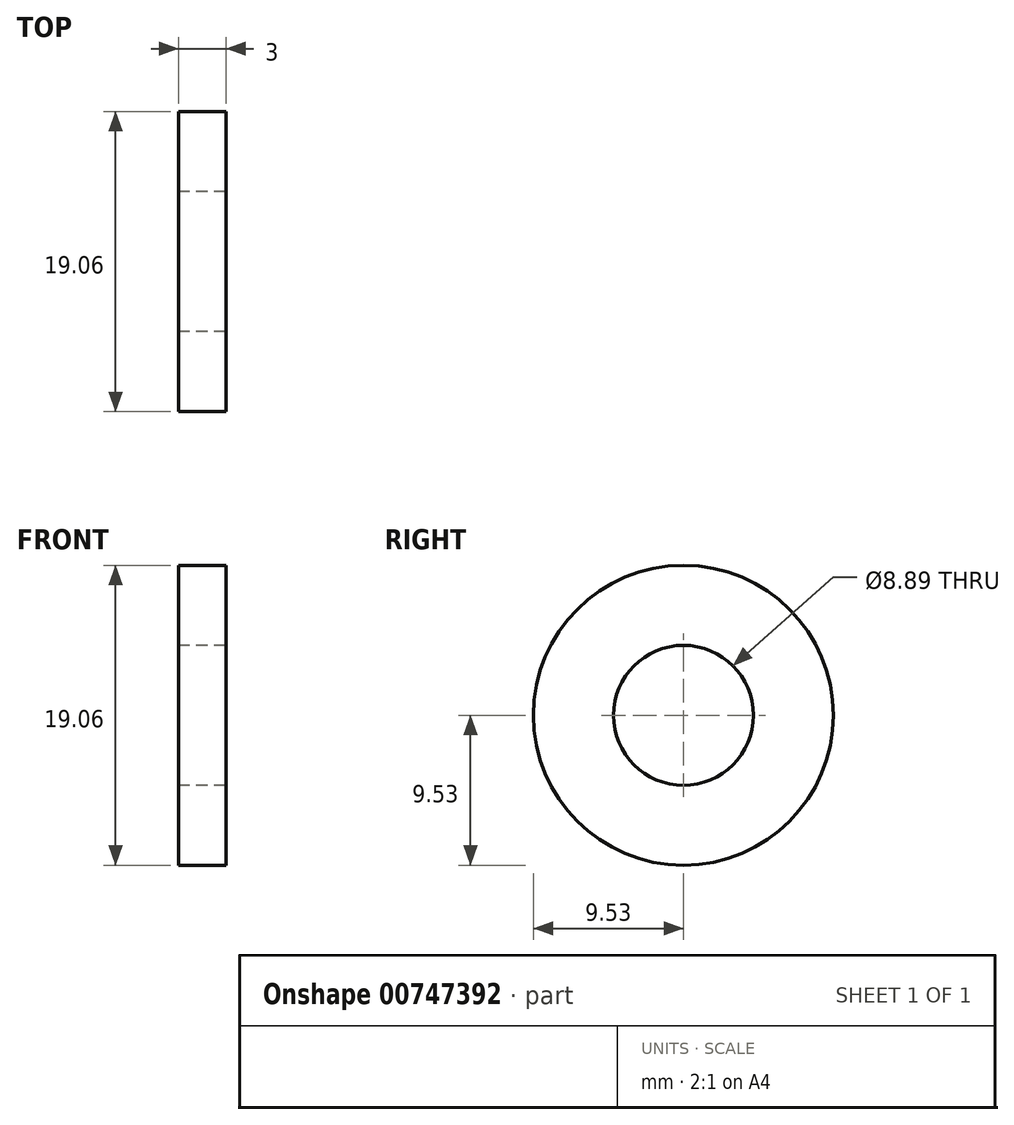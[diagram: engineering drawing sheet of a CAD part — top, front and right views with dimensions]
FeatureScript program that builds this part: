
annotation { "Feature Type Name" : "Feature", "Feature Type Description" : "" }
export const myFeature = defineFeature(function(context is Context, id is Id, definition is map)
    precondition{}
    {
        {
            var Q0;
            Q0=qCreatedBy(makeId("Right.planeOp"),FACE);
            var sketch = newSketch(context, id + "F0", { "sketchPlane" : qUnion([Q0])});
            skCircle(sketch, "E0", {"center": v(0, 0) * mm, "radius": 9.53 * mm});
            skSolve(sketch);
        }
        {
            var Q0;
            Q0=makeQuery(id+"F0.imprint","IMPRINT",FACE,{"disambiguationData":[TD([[makeQuery(id+"F0.imprint","IMPRINT",EDGE,{"derivedFrom":sQuery(id+"F0.wireOp",EDGE,"E0")}),1.0]])]});
            extrude(context, id + "F1", {"entities" : qUnion([Q0]), "depth" : 3 * mm, "offsetDistance" : 25.4 * mm});
        }
        {
            var Q0;
            Q0=qCreatedBy(makeId("Right.planeOp"),FACE);
            var sketch = newSketch(context, id + "F2", { "sketchPlane" : qUnion([Q0])});
            skCircle(sketch, "E1", {"center": v(0, 0) * mm, "radius": 4.45 * mm});
            skSolve(sketch);
        }
        {
            var Q0;
            Q0=makeQuery(id+"F2.imprint","IMPRINT",FACE,{"disambiguationData":[TD([[makeQuery(id+"F2.imprint","IMPRINT",EDGE,{"derivedFrom":sQuery(id+"F2.wireOp",EDGE,"E1")}),1.0]])]});
            extrude(context, id + "F3", {"entities" : qUnion([Q0]), "operationType" : NewBodyOperationType.REMOVE, "depth" : 3 * mm, "offsetDistance" : 25.4 * mm});
        }
    });
